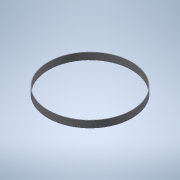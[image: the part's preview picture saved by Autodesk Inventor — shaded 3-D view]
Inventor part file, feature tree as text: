
AUTODESK INVENTOR PART (.ipt)
format: ipt  version: 2021 (Build 250183000, 183)  size: 215,040 bytes
history: native  units: mm
features: extrude x1, sketch x1
ambient origin geometry x8: Origin, YZ Plane, XZ Plane, XY Plane, X Axis, Y Axis, Z Axis, Center Point
bodies: Body1 (feature_tree)
feature tree (2):
  extrude  "Extrusion3"  Depth=50.0mm
  sketch  "Sketch1"  dims[d3=7.5mm d6=30.0mm d7=3.5mm d8=3.5mm d26=8.25mm d27=33.5mm d28=7.5mm d43=4.0mm d44=50.0mm d45=0.0mm]
